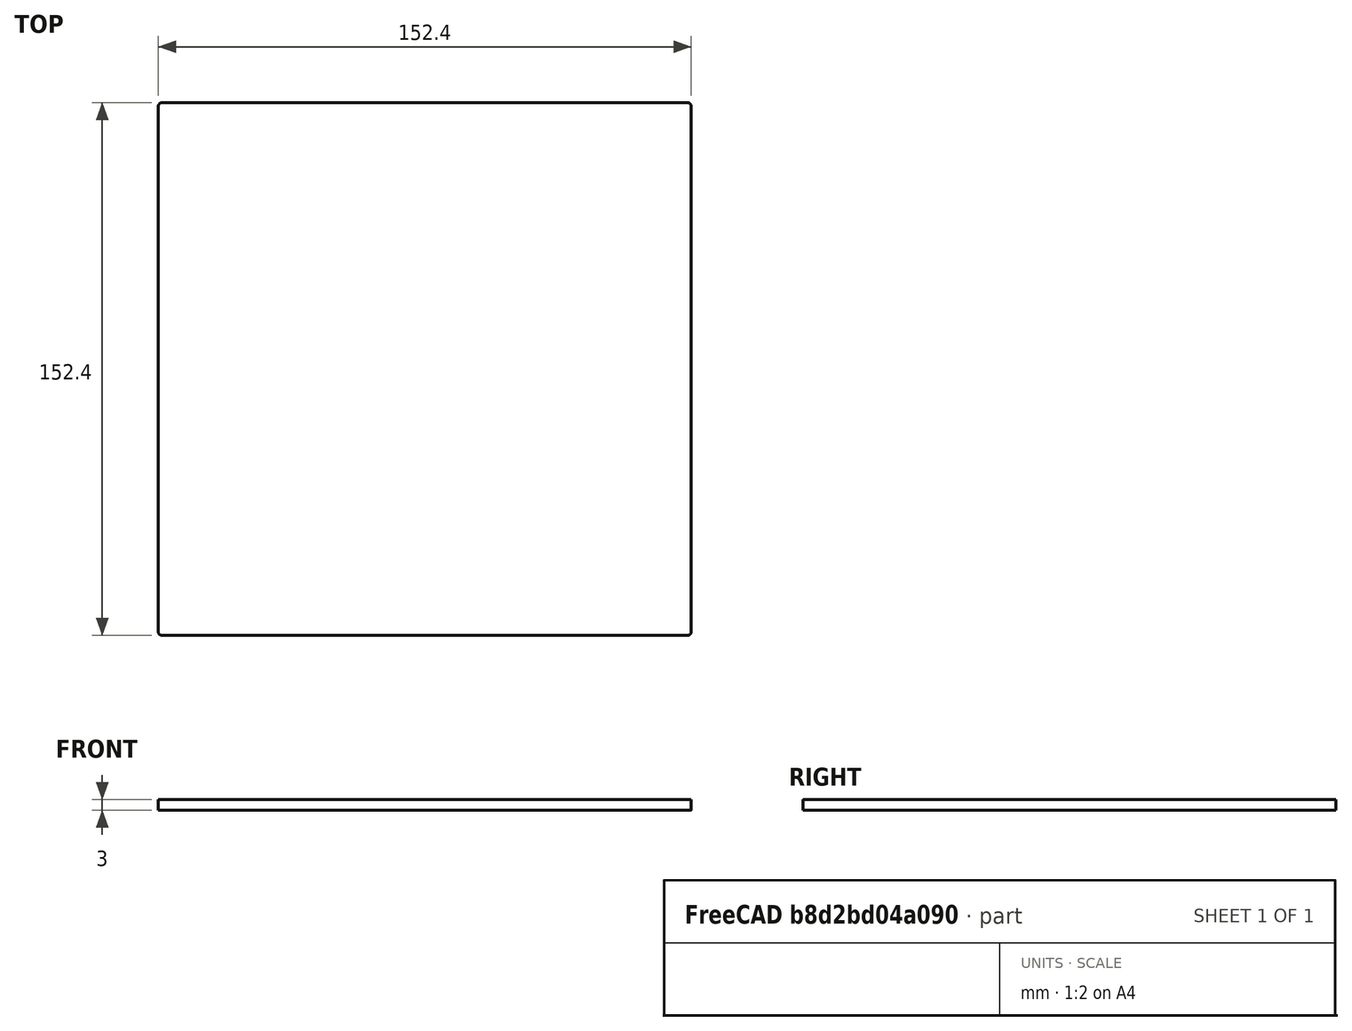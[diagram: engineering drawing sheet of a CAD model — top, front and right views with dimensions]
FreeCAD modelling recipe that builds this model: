
FCSTD DOCUMENT  (FreeCAD 0.20R29603 (Git))
Label: 6in_x_6in
License: All rights reserved
LicenseURL: http://en.wikipedia.org/wiki/All_rights_reserved
objects: Spreadsheet::Sheet×1, Sketcher::SketchObject×1, PartDesign::Pad×1, PartDesign::Body×1
note: 4 computed .brp shape members not serialized (recipe doc carries the construction recipe); baked Part::Feature solids carry a one-line shape summary decoded from their .brp

FEATURE [Spreadsheet::Sheet] Spreadsheet
  cells = A2=Length; B2(Length)==6in; A3=Width; B3(Width)==6in; A4=Thickness; B4(Thickness)==3mm; A5=FilletRadius; B5(FilletRadius)==1mm
FEATURE [Sketcher::SketchObject] Sketch
  FullyConstrained = true
  MapMode = 5
  Support = -> [XY_Plane]
  expr: Constraints[19] = Spreadsheet.FilletRadius
  expr: Constraints[21] = Spreadsheet.Length
  expr: Constraints[22] = Spreadsheet.Width
  sketch-geometry (10):
    g0: ArcOfCircle CenterX=-75.2 CenterY=75.2 CenterZ=0 NormalX=0 NormalY=0 NormalZ=1 AngleXU=0 Radius=1 StartAngle=1.5708 EndAngle=3.14159
    g1: LineSegment StartX=-75.2 StartY=76.2 StartZ=0 EndX=75.2 EndY=76.2 EndZ=0
    g2: ArcOfCircle CenterX=75.2 CenterY=75.2 CenterZ=0 NormalX=0 NormalY=0 NormalZ=1 AngleXU=0 Radius=1 StartAngle=-9e-16 EndAngle=1.5708
    g3: LineSegment StartX=76.2 StartY=75.2 StartZ=0 EndX=76.2 EndY=-75.2 EndZ=0
    g4: ArcOfCircle CenterX=75.2 CenterY=-75.2 CenterZ=0 NormalX=0 NormalY=0 NormalZ=1 AngleXU=0 Radius=1 StartAngle=4.71239 EndAngle=6.28319
    g5: LineSegment StartX=75.2 StartY=-76.2 StartZ=0 EndX=-75.2 EndY=-76.2 EndZ=0
    g6: ArcOfCircle CenterX=-75.2 CenterY=-75.2 CenterZ=0 NormalX=0 NormalY=0 NormalZ=1 AngleXU=0 Radius=1 StartAngle=3.14159 EndAngle=4.71239
    g7: LineSegment StartX=-76.2 StartY=-75.2 StartZ=0 EndX=-76.2 EndY=75.2 EndZ=0
    g8: GeomPoint X=-76.2 Y=76.2 Z=0
    g9: GeomPoint X=76.2 Y=-76.2 Z=0
  constraints (23):
    c: Tangent(g0,g1) = 1.5708
    c: Tangent(g1,g2) = 1.5708
    c: Tangent(g2,g3) = 1.5708
    c: Tangent(g3,g4) = 1.5708
    c: Tangent(g4,g5) = 1.5708
    c: Tangent(g5,g6) = 1.5708
    c: Tangent(g6,g7) = 1.5708
    c: Tangent(g7,g0) = 1.5708
    c: Horizontal(g1)
    c: Horizontal(g5)
    c: Vertical(g3)
    c: Vertical(g7)
    c: Equal(g0,g2)
    c: Equal(g2,g4)
    c: Equal(g4,g6)
    c: PointOnObject(g8,g1)
    c: PointOnObject(g8,g7)
    c: PointOnObject(g9,g3)
    c: PointOnObject(g9,g5)
    c: Radius(g4) = 1
    c: Symmetric(g8,g9,g-1)
    c: DistanceX(g6,g3) = 152.4
    c: DistanceY(g4,g1) = 152.4
FEATURE [PartDesign::Pad] Pad
  Direction = (0,0,1)
  Length = 3
  Length2 = 10
  Profile = -> Sketch
  ReferenceAxis = -> Sketch [N_Axis]
  Type = 0
  expr: Length = Spreadsheet.Thickness
FEATURE [PartDesign::Body] Body
  Group = -> [Sketch,Pad]
  Origin = -> Origin
  Tip = -> Pad
